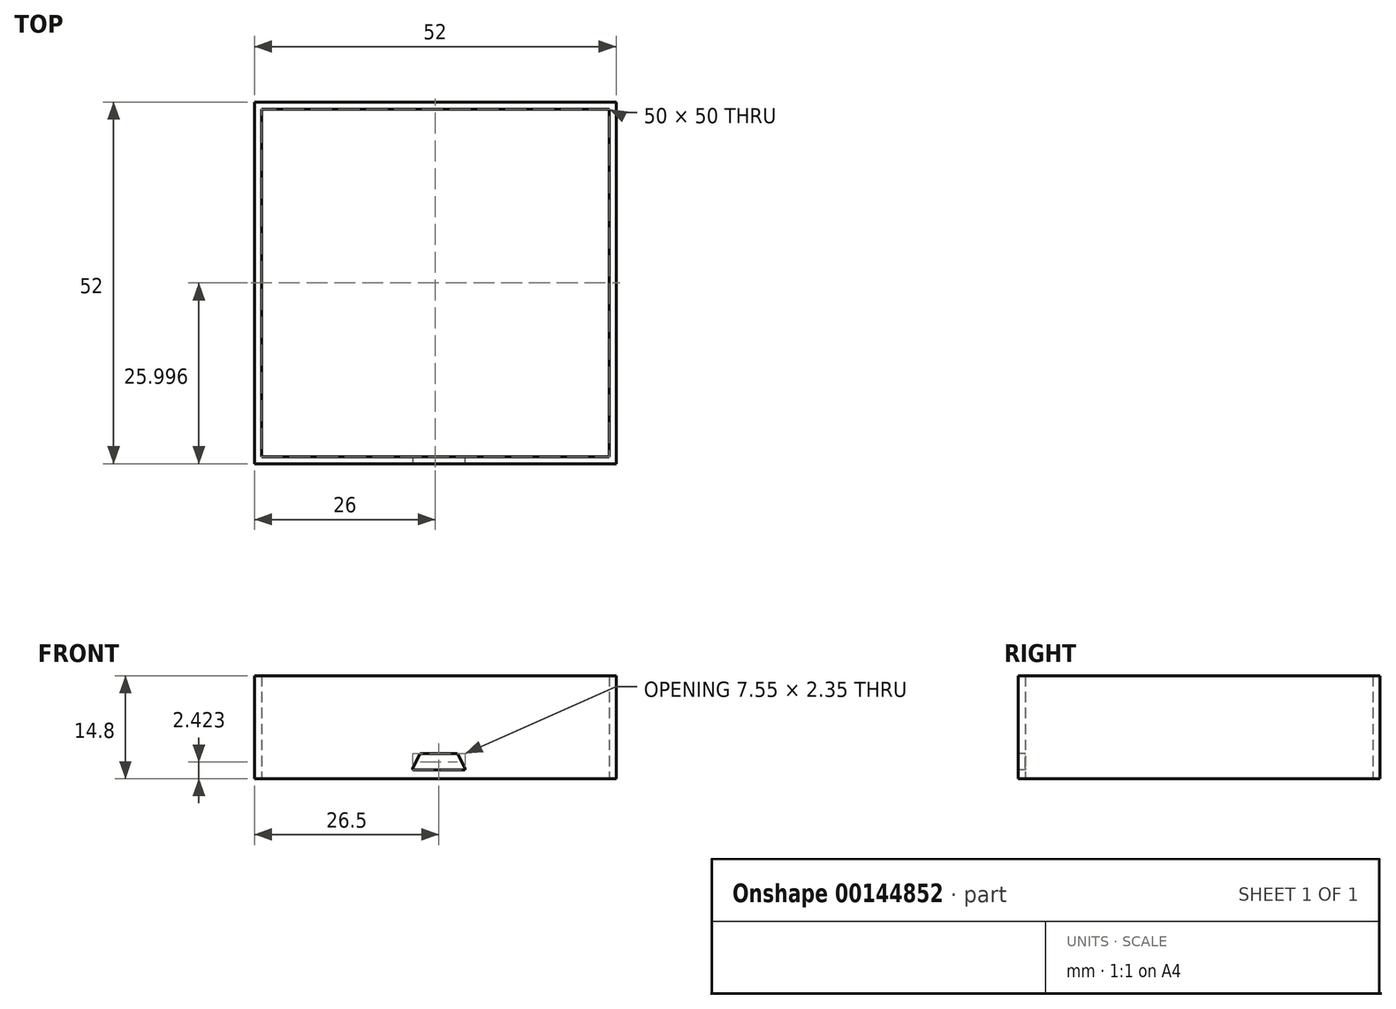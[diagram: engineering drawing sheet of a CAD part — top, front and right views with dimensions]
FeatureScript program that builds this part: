
annotation { "Feature Type Name" : "Feature", "Feature Type Description" : "" }
export const myFeature = defineFeature(function(context is Context, id is Id, definition is map)
    precondition{}
    {
        {
            var Q0;
            Q0=qCreatedBy(makeId("Top.planeOp"),FACE);
            var sketch = newSketch(context, id + "F0", { "sketchPlane" : qUnion([Q0])});
            skLineSegment(sketch, "E0.bottom", {"start": v(47.3, 5.2) * mm, "end": v(-2.7, 5.2) * mm});
            skLineSegment(sketch, "E0.top", {"start": v(47.3, -44.8) * mm, "end": v(-2.7, -44.8) * mm});
            skLineSegment(sketch, "E0.left", {"start": v(47.3, 5.2) * mm, "end": v(47.3, -44.8) * mm});
            skLineSegment(sketch, "E0.right", {"start": v(-2.7, 5.2) * mm, "end": v(-2.7, -44.8) * mm});
            skLineSegment(sketch, "E1.0", {"start": v(48.3, 6.2) * mm, "end": v(-3.7, 6.2) * mm});
            skLineSegment(sketch, "E1.1", {"start": v(48.3, 6.2) * mm, "end": v(48.3, -45.8) * mm});
            skLineSegment(sketch, "E1.2", {"start": v(48.3, -45.8) * mm, "end": v(-3.7, -45.8) * mm});
            skLineSegment(sketch, "E1.3", {"start": v(-3.7, 6.2) * mm, "end": v(-3.7, -45.8) * mm});
            skSolve(sketch);
        }
        {
            var Q0;
            Q0 = qSketchRegion(id + "F0", true);
            var Q1;
            Q1=makeQuery(id+"F0.imprint","IMPRINT",FACE,{"disambiguationData":[TD([[makeQuery(id+"F0.imprint","IMPRINT",EDGE,{"derivedFrom":sQuery(id+"F0.wireOp",EDGE,"E0.bottom")}),-1.0]])]});
            extrude(context, id + "F4", {"entities" : qUnion([Q0, Q1]), "depth" : 14.8 * mm});
        }
        {
            var Q0;
            Q0=makeQuery(id+"F4.opExtrude","SWEPT_FACE",FACE,{"disambiguationData":[OSD([sQuery(id+"F0.wireOp",EDGE,"E1.2")])]});
            var sketch = newSketch(context, id + "F1", { "sketchPlane" : qUnion([Q0])});
            skPoint(sketch, "E2.firstSnap0", {"position": v(22.3, 0) * mm});
            skLineSegment(sketch, "E2.bottom", {"start": v(22.3, 1.25) * mm, "end": v(26.7, 1.25) * mm});
            skLineSegment(sketch, "E2.top", {"start": v(22.8, 3.6) * mm, "end": v(25.5, 3.6) * mm});
            skLineSegment(sketch, "E3.bottom", {"start": v(22.3, 1.25) * mm, "end": v(18.9, 1.25) * mm});
            skLineSegment(sketch, "E3.top", {"start": v(22.8, 3.6) * mm, "end": v(20.1, 3.6) * mm});
            skPoint(sketch, "E4", {"position": v(25.5, 3.6) * mm});
            skPoint(sketch, "E5", {"position": v(20.1, 3.6) * mm});
            skLineSegment(sketch, "E6", {"start": v(25.5, 3.6) * mm, "end": v(26.7, 1.25) * mm});
            skLineSegment(sketch, "E7", {"start": v(20.1, 3.6) * mm, "end": v(18.9, 1.25) * mm});
            skSolve(sketch);
        }
        {
            var Q0;
            Q0=makeQuery(id+"F1.imprint","IMPRINT",FACE,{"disambiguationData":[TD([[makeQuery(id+"F1.imprint","IMPRINT",EDGE,{"derivedFrom":sQuery(id+"F1.wireOp",EDGE,"E2.bottom")}),1.0]])]});
            extrude(context, id + "F2", {"entities" : qUnion([Q0]), "operationType" : NewBodyOperationType.REMOVE, "endBound" : BoundingType.UP_TO_NEXT, "oppositeDirection" : true, "depth" : 25 * mm});
        }
        {
            var Q0;
            Q0=makeQuery(id+"F2.boolean.opBoolean","COPY",EDGE,{"derivedFrom":makeQuery(id+"F2.opExtrude","SWEPT_EDGE",EDGE,{"disambiguationData":[OSD([sQuery(id+"F1.wireOp",EDGE,"E3.bottom"),sQuery(id+"F1.wireOp",EDGE,"E7")])]})});
            var Q1;
            Q1=makeQuery(id+"F2.boolean.opBoolean","COPY",EDGE,{"derivedFrom":makeQuery(id+"F2.opExtrude","SWEPT_EDGE",EDGE,{"disambiguationData":[OSD([sQuery(id+"F1.wireOp",EDGE,"E2.bottom"),sQuery(id+"F1.wireOp",EDGE,"E6")])]})});
            var Q2;
            Q2=makeQuery(id+"F2.boolean.opBoolean","COPY",EDGE,{"derivedFrom":makeQuery(id+"F2.opExtrude","SWEPT_EDGE",EDGE,{"disambiguationData":[OSD([sQuery(id+"F1.wireOp",EDGE,"E2.top"),sQuery(id+"F1.wireOp",EDGE,"E6")])]})});
            var Q3;
            Q3=makeQuery(id+"F2.boolean.opBoolean","COPY",EDGE,{"derivedFrom":makeQuery(id+"F2.opExtrude","SWEPT_EDGE",EDGE,{"disambiguationData":[OSD([sQuery(id+"F1.wireOp",EDGE,"E3.top"),sQuery(id+"F1.wireOp",EDGE,"E7")])]})});
            fillet(context, id + "F3", {"entities" : qUnion([Q0, Q1, Q2, Q3]), "radius" : 0.2 * mm, "tangentPropagation" : true, "allowEdgeOverflow" : false});
        }
    });
